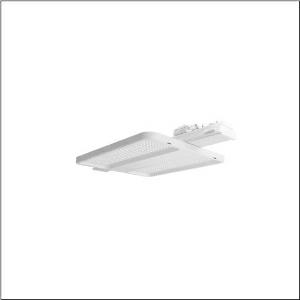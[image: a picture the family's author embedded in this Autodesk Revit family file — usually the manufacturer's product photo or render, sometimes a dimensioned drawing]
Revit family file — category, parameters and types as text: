
# Revit family: highbay_11_fur_licross_r__tragschiene_midi_51hn11da4fla_28e0
name_source: partatom
category: Lighting Fixtures
units: mm (PartAtom-declared; Revit-internal decimal feet)

## family parameters
Cut with Voids When Loaded = No
Host = Face
Light Source = No
Part Type = Normal
Room Calculation Point = No
Round Connector Dimension = Use Diameter
Shared = No

## types (1)
- --- (1 x LED, 15000 lm, 73.2 W, 4000K)
    Apparent Load = 73 VA
    CIE Flux Codes = 85 97 100 100 100
    Color Rendering = 80
    Color Temperature = 4000K
    Default Elevation = 1800 mm
    Description = high bay luminaire Highbay 11 for Licross® trunking rail midi; direct symmetric narrow distribution, light control with lens of PMMA; UGR ≤ 22 (X = 4H | Y = 8H | S = 0.25H | reflection values 70/50/20); luminous flux: 15.000lm; light colour: 840, colour temperature: 4000K, MacAdam ≤ 2 SDCM (initial), colour rendering: CRI > 80; luminous efficacy: 204,9lm/W; rated service life: 100.000h (L95/B50) at AT= 25°C; control: DALI 2; luminaire connection: plug, 5-pole, with phase selectionmains connection: 230..240V, AC 50/60Hz; connected load: 73,2W; protection rating (complete): IP64; insulation class (complete): insulation class I (protective earthing); protection symbol: D; impact resistance: IK07; certification: CE, ENEC, VDE, UKCA; internal wiring halogen-free; luminaire corresponds to IFS (International Featured Standards) requirements for safety and quality in the food industry; LABS conformity tested according to VDMA 24364:2018-05; housing frame of high-performance plastic PA6, matt traffic white (RAL 9016); cover of PMMA; fixing on rail side of steel, galvanised, white; blank cover of PC/ABS, traffic white (RAL 9016); dimension (LxWxH): 750 x 442 x 71mm; permissible operating ambient temperature: -40..+55°C (reducing of maximum allowable ambient temperature of 5°C with ceiling mounting); packaging unit: 1 piece
    Height = 72 mm  [stored 0.23622 ft]
    Lamp = 1 x LED
    Lamp Light Flux = 15000 lm
    Lamp Power = 73.2 W
    Lamp count = 1
    Length = 474 mm
    Luminous efficacy = 205 lm/W
    Manufacturer = Siteco
    ModVariant = No
    Model = 51HN11DA4FLA
    Mounting Place = Ceiling
    Mounting Type = Pendant
    Number of Poles = 1
    OnlyDefault = Yes
    Power Factor = 1
    Product Name = Highbay 11 für Licross® Tragschiene midi
    Product group = high bay luminaire
    ProductGroupID = 901
    Protection Class = Protection class I
    Protection Degree = IP 64
    RLX_Detail_Level = 1
    RLX_Emergency_Light_Flux = 0 lm
    RLX_Emergency_Type = 0
    RLX_Emergency_Type_DB = No
    RlxData = <blob elided: 17121 chars, md5=d01eefbf>
    Socket = socket
    Standby Power = 0 W
    System Light Flux = 15000 lm
    System Power = 73 W
    Type Comments = factory setting: luminous flux: 100 % | dim-lin: 254 | 339 mA
    Type Image = l_1363258.jpg
    URL = http://relux.com
    VarID = @adj_023049
    Voltage = 0 V
    Weight = 0.00 kg
    Width = 442 mm

note: [stored X ft] marks values corroborated as IEEE doubles in the binary element streams (Revit-internal decimal feet)

## geometry (parser evidence)
native form markers: Blend x4, Sweep x12
no freeform markers — native parametric forms only
